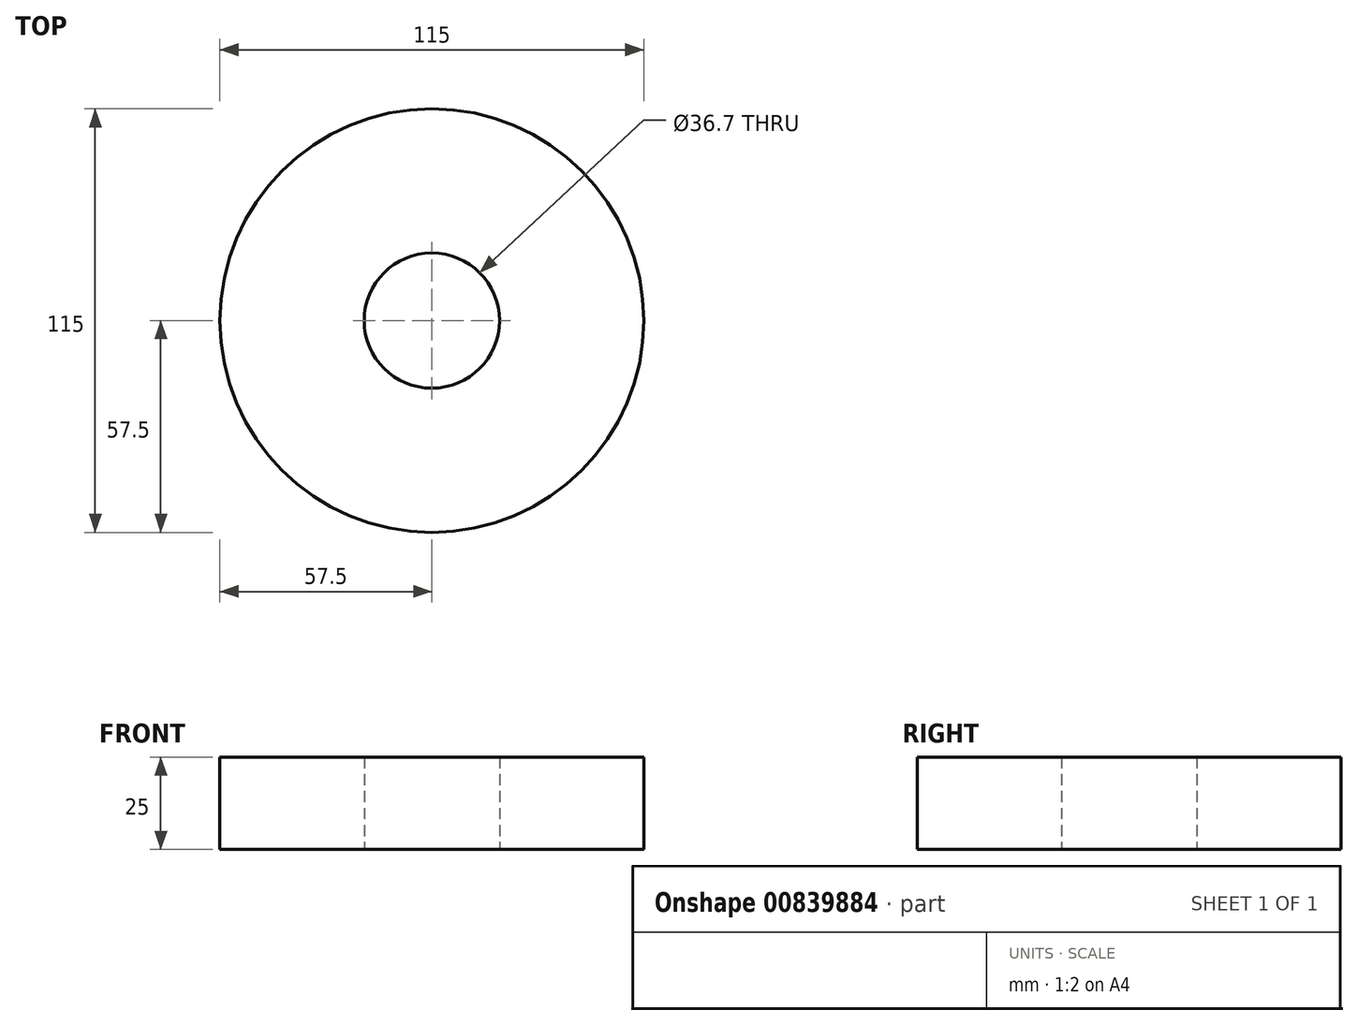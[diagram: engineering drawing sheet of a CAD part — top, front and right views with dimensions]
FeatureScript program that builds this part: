
annotation { "Feature Type Name" : "Feature", "Feature Type Description" : "" }
export const myFeature = defineFeature(function(context is Context, id is Id, definition is map)
    precondition{}
    {
        {
            var Q0;
            Q0=qCreatedBy(makeId("Top.planeOp"),FACE);
            var sketch = newSketch(context, id + "F0", { "sketchPlane" : qUnion([Q0])});
            skCircle(sketch, "E0", {"center": v(0, 0) * mm, "radius": 18.35 * mm});
            skCircle(sketch, "E1", {"center": v(0, 0) * mm, "radius": 57.5 * mm});
            skSolve(sketch);
        }
        {
            var Q0;
            Q0=qSketchRegion(id+"F0",true);
            extrude(context, id + "F1", {"entities" : qUnion([Q0]), "depth" : 25 * mm, "offsetDistance" : 25 * mm});
        }
    });
